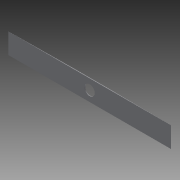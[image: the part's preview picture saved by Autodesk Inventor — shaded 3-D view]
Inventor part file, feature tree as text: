
AUTODESK INVENTOR PART (.ipt)
format: ipt  version: 2014 SP2 (Build 180246200, 246)  size: 79,872 bytes
history: native  units: mm
features: chamfer x2, extrude x1, sketch x1
ambient origin geometry x8: Origin, YZ Plane, XZ Plane, XY Plane, X Axis, Y Axis, Z Axis, Center Point
bodies: Solid1 (feature_tree)
feature tree (4):
  extrude  "Extrusion1"  Depth=32.0mm
  chamfer  "Chamfer1"  Distance=1.0mm
  chamfer  "Chamfer2"  Distance=1.0mm Angle=45.0deg
  sketch  "Sketch1"  dims[d0=254.0mm d1=32.0mm d2=1.0mm d3=0.0mm d4=100.0mm d5=1.0mm d6=45.0deg d7=100.0mm d8=1.0mm d9=45.0deg d10=16.0mm d11=127.0mm d12=16.0mm]
